# Revit family: Accessories-Teknion-RHACT_Countertop-R2018
name_source: partatom
category: Furniture
revit_build: Autodesk Revit 2018 (Build: 20190510_1515(x64)
units: mm (PartAtom-declared; Revit-internal decimal feet)

## family parameters
Always vertical = Yes
Cut with Voids When Loaded = No
OmniClass Number = 23.40.20.00
OmniClass Title = General Furniture and Specialties
Room Calculation Point = No
Shared = Yes
Work Plane-Based = No

## types (4) — shared parameters
Assembly Code = E2020200
Counter Finish = Foundation Laminate - Teknion - HX - Costal Elm
For Additional Finishes please visit = https://assets.teknion.com
Manufacturer = Teknion
Manufacturer Fax = 416.661.4586
Part Number = RHACT
Product Documentation Link = https://www.teknion.com
Product Line = Modular Cabinets
Product Page URL = https://www.teknion.com
Series = Modular Cabinets
Sustainability Data = https://www.teknion.com
To render please download texture images found here = https://assets.teknion.com
URL = www.teknion.com
Unit Weight URL = http://www.teknion.com
Warranty = http://www.teknion.com

## per-type parameters (varying)
| type | Counter Material Note | Description | Height | Model | Water Resistant |
| Standard Option, 35" Datum Height | Select a Foundation Laminate or Flintwood material for Counter Finish | Countertop, Standard Option | 35 " | RHACTS_____ | No |
| Water Resistant Option, 35" Datum height | Select a Foundation Laminate material for Counter Finish | Countertop, Water Resistant Option | 35 " | RHACTW_____ | Yes |
| Standard Option, 33" Datum Height | Select a Foundation Laminate or Flintwood material for Counter Finish | Countertop, Standard Option | 33 " | RHACTS_____ | No |
| Water Resistant Option, 33" Datum Height | Select a Foundation Laminate material for Counter Finish | Countertop, Water Resistant Option | 33 " | RHACTW_____ | Yes |

## geometry (parser evidence)
native form markers: Sweep x2
no freeform markers — native parametric forms only
